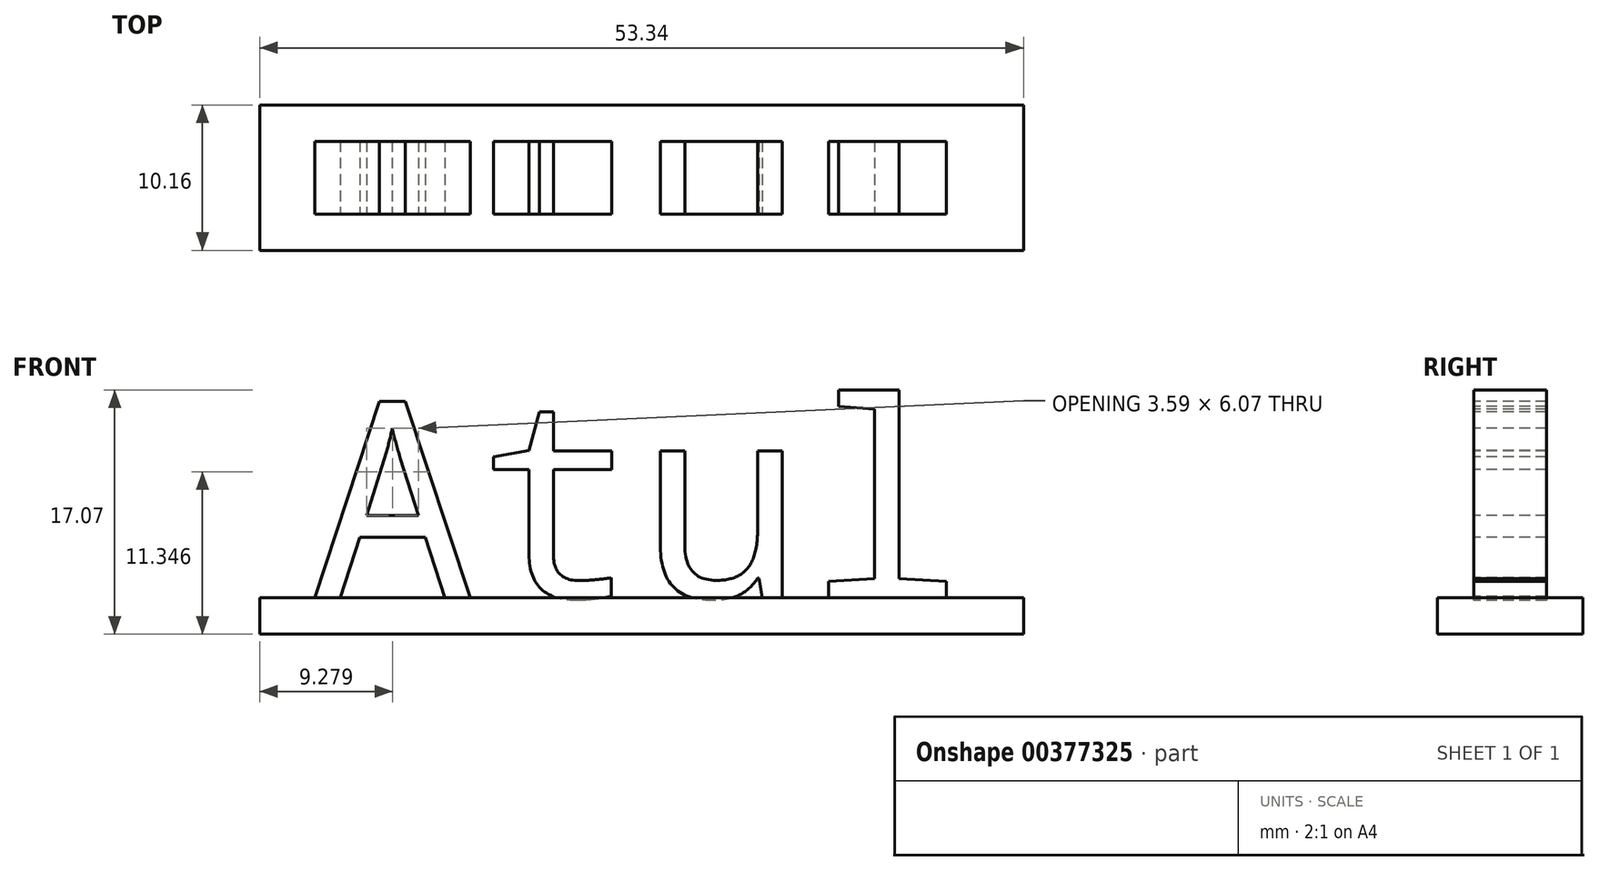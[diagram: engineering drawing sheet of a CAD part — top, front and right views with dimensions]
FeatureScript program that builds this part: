
annotation { "Feature Type Name" : "Feature", "Feature Type Description" : "" }
export const myFeature = defineFeature(function(context is Context, id is Id, definition is map)
    precondition{}
    {
        {
            var Q0;
            Q0=qCreatedBy(makeId("Front.planeOp"),FACE);
            var sketch = newSketch(context, id + "F0", { "sketchPlane" : qUnion([Q0])});
            skText(sketch, "E0", { "text": "Atul\n", "fontName": "DroidSansMono.ttf"});
            const initialGuessF0  = {"E0": [-0.04726, 0, 1, 0, 0.01377]};
            skSetInitialGuess(sketch, initialGuessF0);
            skSolve(sketch);
        }
        {
            var Q0;
            Q0=qCreatedBy(makeId("Top.planeOp"),FACE);
            var sketch = newSketch(context, id + "F1", { "sketchPlane" : qUnion([Q0])});
            skLineSegment(sketch, "E1.bottom", {"start": v(0, 0) * mm, "end": v(-50.8, 0) * mm});
            skLineSegment(sketch, "E1.top", {"start": v(0, 7.62) * mm, "end": v(-50.8, 7.62) * mm});
            skLineSegment(sketch, "E1.left", {"start": v(0, 0) * mm, "end": v(0, 7.62) * mm});
            skLineSegment(sketch, "E1.right", {"start": v(-50.8, 0) * mm, "end": v(-50.8, 7.62) * mm});
            skLineSegment(sketch, "E2.top", {"start": v(0, -2.54) * mm, "end": v(-50.8, -2.54) * mm});
            skLineSegment(sketch, "E2.left", {"start": v(0, 0) * mm, "end": v(0, -2.54) * mm});
            skLineSegment(sketch, "E2.right", {"start": v(-50.8, 0) * mm, "end": v(-50.8, -2.54) * mm});
            skLineSegment(sketch, "E3.bottom", {"start": v(0, 7.62) * mm, "end": v(2.54, 7.62) * mm});
            skLineSegment(sketch, "E3.top", {"start": v(0, -2.54) * mm, "end": v(2.54, -2.54) * mm});
            skLineSegment(sketch, "E3.left", {"start": v(0, 7.62) * mm, "end": v(0, -2.54) * mm});
            skLineSegment(sketch, "E3.right", {"start": v(2.54, 7.62) * mm, "end": v(2.54, -2.54) * mm});
            skSolve(sketch);
        }
        {
            var Q0;
            Q0=makeQuery(id+"F0.imprint","IMPRINT",FACE,{"disambiguationData":[TD([[makeQuery(id+"F0.imprint","IMPRINT",EDGE,{"derivedFrom":sQuery(id+"F0.wireOp",EDGE,"E0.sketch_text.stroke-43")}),-1.0]])]});
            var Q1;
            Q1=makeQuery(id+"F0.imprint","IMPRINT",FACE,{"disambiguationData":[TD([[makeQuery(id+"F0.imprint","IMPRINT",EDGE,{"derivedFrom":sQuery(id+"F0.wireOp",EDGE,"E0.sketch_text.stroke-29")}),-1.0]])]});
            var Q2;
            Q2=makeQuery(id+"F0.imprint","IMPRINT",FACE,{"disambiguationData":[TD([[makeQuery(id+"F0.imprint","IMPRINT",EDGE,{"derivedFrom":sQuery(id+"F0.wireOp",EDGE,"E0.sketch_text.stroke-13")}),-1.0]])]});
            var Q3;
            Q3=makeQuery(id+"F0.imprint","IMPRINT",FACE,{"disambiguationData":[TD([[makeQuery(id+"F0.imprint","IMPRINT",EDGE,{"derivedFrom":sQuery(id+"F0.wireOp",EDGE,"E0.sketch_text.stroke-0")}),-1.0]])]});
            extrude(context, id + "F2", {"entities" : qUnion([Q0, Q1, Q2, Q3]), "depth" : -5.08 * mm});
        }
        {
            var Q0;
            {var subQ0=sQuery(id+"F1.wireOp",EDGE,"E1.bottom");Q0=makeQuery(id+"F1.imprint","IMPRINT",FACE,{"disambiguationData":[TD([[makeQuery(id+"F1.imprint","IMPRINT",EDGE,{"derivedFrom":subQ0}),1.0]])]});}
            var Q1;
            {var subQ0=sQuery(id+"F1.wireOp",EDGE,"E1.top");Q1=makeQuery(id+"F1.imprint","IMPRINT",FACE,{"disambiguationData":[TD([[makeQuery(id+"F1.imprint","IMPRINT",EDGE,{"derivedFrom":subQ0}),1.0]])]});}
            var Q2;
            {var subQ3=sQuery(id+"F1.wireOp",EDGE,"E3.bottom");Q2=makeQuery(id+"F1.imprint","IMPRINT",FACE,{"disambiguationData":[TD([[makeQuery(id+"F1.imprint","IMPRINT",EDGE,{"derivedFrom":subQ3}),-1.0]])]});}
            extrude(context, id + "F3", {"entities" : qUnion([Q0, Q1, Q2]), "depth" : -2.54 * mm});
        }
    });
